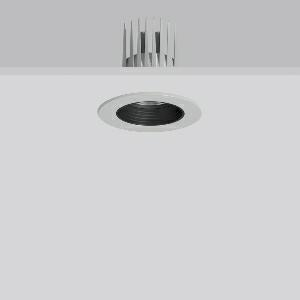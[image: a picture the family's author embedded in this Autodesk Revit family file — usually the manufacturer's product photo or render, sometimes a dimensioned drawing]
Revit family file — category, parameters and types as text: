
# Revit family: heledon_mini_e_901751_004_76_5e60
name_source: partatom
category: Lighting Fixtures
units: mm (PartAtom-declared; Revit-internal decimal feet)

## family parameters
Cut with Voids When Loaded = No
Host = Face
Light Source = No
Part Type = Normal
Room Calculation Point = No
Round Connector Dimension = Use Diameter
Shared = No

## types (1)
- HELEDON mini E (1 x LED Modul 930, 3150 lm, 3000)
    Apparent Load = 29 VA
    Approval mark = CE
    CIE Flux Codes = 99 100 100 100 100
    Color Rendering = 90
    Color Temperature = 3000
    Default Elevation = 1800 mm
    Description = Series: HELEDON mini
Round recessed downlight. Housing: die-cast aluminium, powder-coated. Black plastic ring and recessed LED to prevent glare from the side. Optical assembly with lens made of plastic (polycarbonate) for the best homogeneous light distribution - can be changed without tools. Best colour rendering index Ra>90. Suitable for Recessed ceiling mounting. Installation without tools thanks to spring fastening system. Including separate LED converter with connecting cable 600 mm.High quality converter without flickering and stroboscopic effect. Through-wiring box (5 pole) available as accessory. The following accessories can be mounted without use of tools: interchangeable lenses, decorative glasses, honeycomb louvre, clear and frosted diffusers, white interchangeable plastic ring. 
Colour: silver
Diameter: 124 mm
Height: 3 mm
Cut-out diameter: 114 mm
Recess height: 170 mm
Luminaire: recess height: 120 mm
Lamp: LED
Socket: without socket
Colour temperature: 3000K
Colour rendering index (CRI): 92
System power: 29 W
Rated luminous flux: 3150 lm
Luminous efficiency: 109 lm/W
Control gear: Converter, dimmable, DALI
Protection class: II
Type of protection: IP 20
    Height = 0 mm  [stored 0 ft]
    Lamp = 1 x LED Modul 930
    Lamp Light Flux = 3150 lm
    Lamp count = 1
    Length = 124 mm  [stored 0.406824 ft]
    Lifetime = 50000 h
    Luminous efficacy = 109 lm/W
    Manufacturer = RZB
    ModVariant = No
    Model = 901751.004.76
    Mounting Place = Ceiling
    Mounting Type = Recessed
    Number of Poles = 1
    OnlyDefault = Yes
    Power Factor = 1
    Product Name = HELEDON mini E
    Product group = Recessed downlights
    ProductGroupID = 402
    Protection Class = Protection class II
    Protection Degree = IP 20
    RLX_Detail_Level = 1
    RLX_Emergency_Light_Flux = 0 lm
    RLX_Emergency_Type = 0
    RLX_Emergency_Type_DB = No
    RlxData = <blob elided: 126693 chars, md5=948c38d3>
    Socket = socket
    Standby Power = 0 W
    System Light Flux = 3150 lm
    System Power = 29 W
    Type Comments = Product without accessories
    Type Image = 901656.004.jpg
    URL = http://relux.com
    VarID = ---
    Voltage = 230 V
    Voltage Range = 220-240 V
    Weight = 0.00 kg
    Width = 0 mm  [stored 0 ft]

note: [stored X ft] marks values corroborated as IEEE doubles in the binary element streams (Revit-internal decimal feet)

## geometry (parser evidence)
native form markers: Blend x4, Sweep x12
no freeform markers — native parametric forms only
